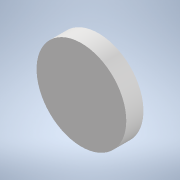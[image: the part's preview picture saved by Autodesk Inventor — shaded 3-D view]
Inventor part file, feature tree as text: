
AUTODESK INVENTOR PART (.ipt)
format: ipt  version: 2020 (Build 240168000, 168)  size: 91,648 bytes
history: native  units: in
note: dims shown in document units (in); Inventor stores cm internally (conversion verified against a paired STEP export)
features: other x3, sketch x1, plane x1, extrude x1, reference x1
ambient origin geometry x8: Origin, YZ Plane, XZ Plane, XY Plane, X Axis, Y Axis, Z Axis, Center Point
bodies: Solid1 (feature_tree)
feature tree (7):
  sketch  "Sketch1"  dims[d0=1.0in d1=0.0in]
  plane  "Work Plane1"
  extrude  "Extrusion1"  [1 undecoded]
  reference  "Reference1"
  other  "<userpath>\Documents\FRC\2020\am-0940a 6 HiGrip wheel REV2.iam"
  other  "am-0940a 6 HiGrip wheel REV2.iam"
  other  "6 wheel tread II_2"
note: 1 required parameter value undecoded (feature->parameter linkage not recoverable at this tier; creation-order binding heuristic only, values carry confidence <= 0.55)
